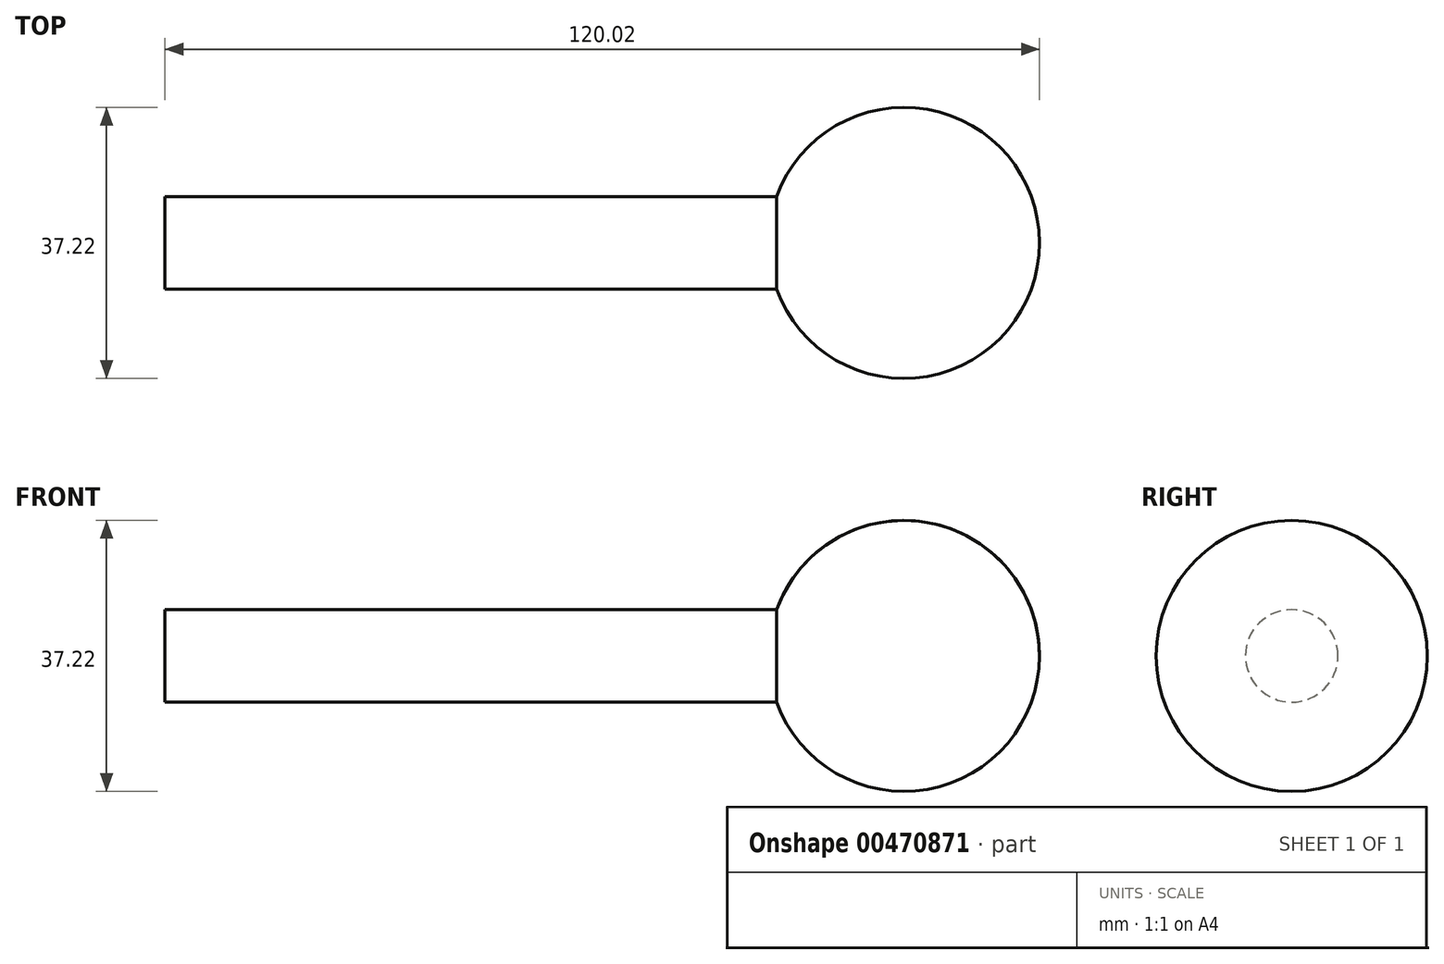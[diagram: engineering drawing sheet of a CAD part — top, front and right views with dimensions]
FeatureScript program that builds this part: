
annotation { "Feature Type Name" : "Feature", "Feature Type Description" : "" }
export const myFeature = defineFeature(function(context is Context, id is Id, definition is map)
    precondition{}
    {
        {
            var Q0;
            Q0=qCreatedBy(makeId("Front.planeOp"),FACE);
            var sketch = newSketch(context, id + "F0", { "sketchPlane" : qUnion([Q0])});
            skLineSegment(sketch, "E0", {"start": v(0, 0) * mm, "end": v(0, 6.35) * mm});
            skLineSegment(sketch, "E1", {"start": v(0, 6.35) * mm, "end": v(101.4, 6.35) * mm});
            skArc(sketch, "E2", {"start": v(120.02, 0) * mm, "mid": v(104.63, 18.33) * mm, "end": v(83.91, 6.35) * mm});
            skLineSegment(sketch, "E3.0", {"start": v(0, 0) * mm, "end": v(82.8, 0) * mm});
            skLineSegment(sketch, "E4", {"start": v(82.8, 0) * mm, "end": v(120.02, 0) * mm});
            skSolve(sketch);
        }
        {
            var Q0;
            {var subQ2=sQuery(id+"F0.wireOp",EDGE,"E0");Q0=makeQuery(id+"F0.imprint","IMPRINT",FACE,{"disambiguationData":[TD([[makeQuery(id+"F0.imprint","IMPRINT",EDGE,{"derivedFrom":subQ2}),-1.0]])]});}
            var Q1;
            Q1=sQuery(id+"F0.wireOp",EDGE,"E3.0");
            revolve(context, id + "F1", {"entities" : qUnion([Q0]), "axis" : qUnion([Q1]), "revolveType" : RevolveType.FULL});
        }
    });
